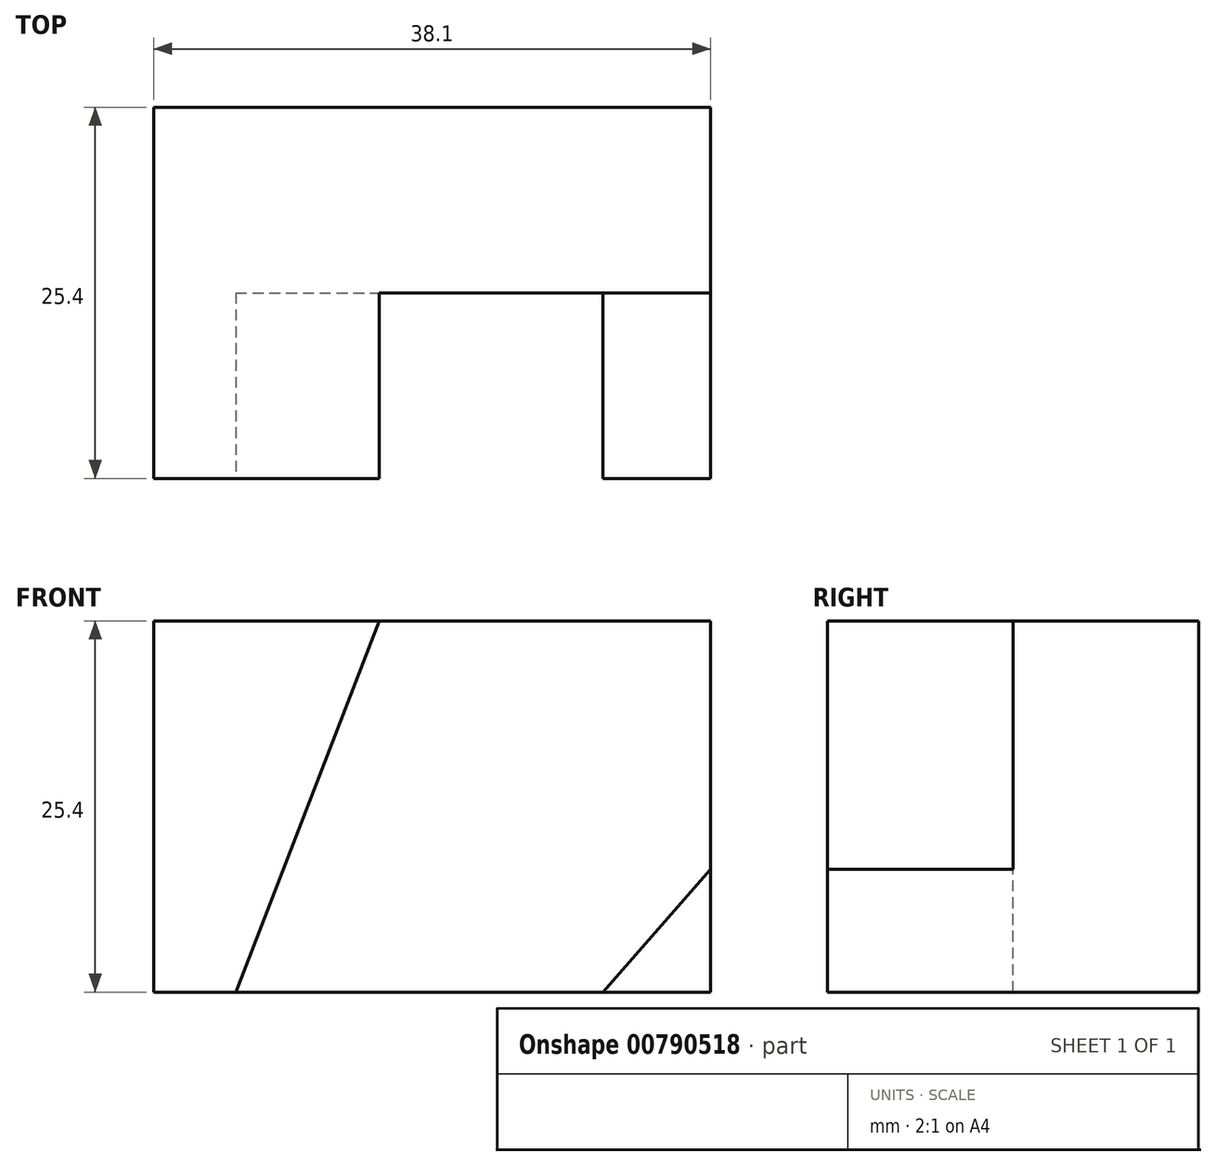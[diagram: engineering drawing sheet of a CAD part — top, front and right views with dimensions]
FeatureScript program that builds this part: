
annotation { "Feature Type Name" : "Feature", "Feature Type Description" : "" }
export const myFeature = defineFeature(function(context is Context, id is Id, definition is map)
    precondition{}
    {
        {
            var Q0;
            Q0=qCreatedBy(makeId("Front.planeOp"),FACE);
            var sketch = newSketch(context, id + "F0", { "sketchPlane" : qUnion([Q0])});
            skLineSegment(sketch, "E0", {"start": v(0, 25.4) * mm, "end": v(0, 0) * mm});
            skLineSegment(sketch, "E1", {"start": v(0, 0) * mm, "end": v(38.1, 0) * mm});
            skLineSegment(sketch, "E2", {"start": v(38.1, 0) * mm, "end": v(38.1, 25.4) * mm});
            skLineSegment(sketch, "E3", {"start": v(0, 25.4) * mm, "end": v(38.1, 25.4) * mm});
            skSolve(sketch);
        }
        {
            var Q0;
            Q0=qSketchRegion(id+"F0",true);
            extrude(context, id + "F1", {"entities" : qUnion([Q0]), "depth" : 25.4 * mm, "offsetDistance" : 25.4 * mm});
        }
        {
            var Q0;
            Q0=makeQuery(id+"F1.opExtrude","CAP_FACE",FACE,{"disambiguationData":[OSD([sQuery(id+"F0.wireOp",EDGE,"E0"),sQuery(id+"F0.wireOp",EDGE,"E1"),sQuery(id+"F0.wireOp",EDGE,"E2"),sQuery(id+"F0.wireOp",EDGE,"E3")])],"isStart":false});
            var sketch = newSketch(context, id + "F2", { "sketchPlane" : qUnion([Q0])});
            skLineSegment(sketch, "E4", {"start": v(5.6, 0) * mm, "end": v(15.43, 25.4) * mm});
            skLineSegment(sketch, "E5", {"start": v(15.43, 25.4) * mm, "end": v(38.1, 25.4) * mm});
            skLineSegment(sketch, "E6", {"start": v(38.1, 25.4) * mm, "end": v(38.1, 0) * mm});
            skLineSegment(sketch, "E7", {"start": v(38.1, 0) * mm, "end": v(30.73, 0) * mm});
            skLineSegment(sketch, "E8", {"start": v(30.73, 0) * mm, "end": v(38.1, 8.4) * mm});
            skSolve(sketch);
        }
        {
            var Q0;
            {var subQ3=sQuery(id+"F2.wireOp",EDGE,"E4");Q0=makeQuery(id+"F2.imprint","IMPRINT",FACE,{"disambiguationData":[TD([[makeQuery(id+"F2.imprint","IMPRINT",EDGE,{"derivedFrom":subQ3}),-1.0]])]});}
            extrude(context, id + "F3", {"entities" : qUnion([Q0]), "operationType" : NewBodyOperationType.REMOVE, "oppositeDirection" : true, "depth" : 12.7 * mm, "offsetDistance" : 25.4 * mm});
        }
    });
